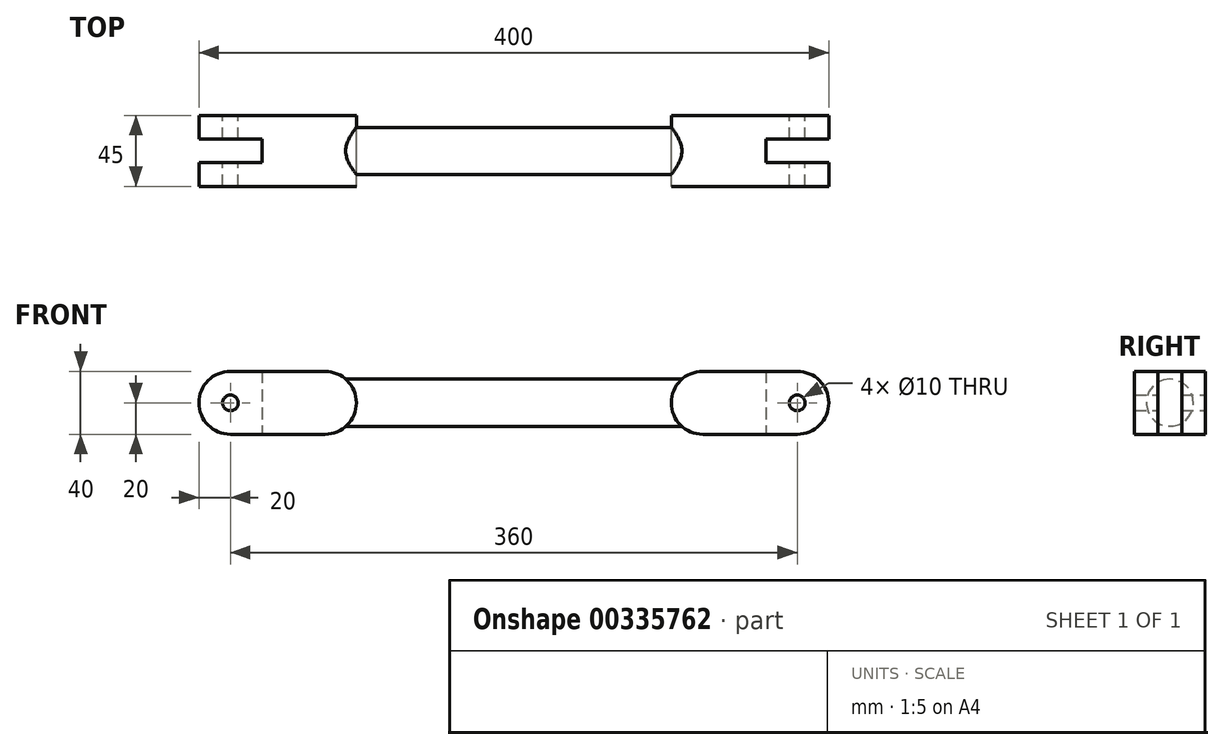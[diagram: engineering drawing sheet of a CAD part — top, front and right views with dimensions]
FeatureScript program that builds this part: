
annotation { "Feature Type Name" : "Feature", "Feature Type Description" : "" }
export const myFeature = defineFeature(function(context is Context, id is Id, definition is map)
    precondition{}
    {
        {
            var Q0;
            Q0=qCreatedBy(makeId("Front.planeOp"),FACE);
            var sketch = newSketch(context, id + "F0", { "sketchPlane" : qUnion([Q0])});
            skCircle(sketch, "E0", {"center": v(-180, 0) * mm, "radius": 20 * mm});
            skCircle(sketch, "E1", {"center": v(-120, 0) * mm, "radius": 20 * mm});
            skLineSegment(sketch, "E2", {"start": v(-180, 20) * mm, "end": v(-120, 20) * mm});
            skLineSegment(sketch, "E3", {"start": v(-180, -20) * mm, "end": v(-120, -20) * mm});
            skLineSegment(sketch, "E4", {"start": v(-180, 0) * mm, "end": v(-120, 0) * mm, "construction": true});
            skPoint(sketch, "E5", {"position": v(-150, 0) * mm});
            skCircle(sketch, "E6", {"center": v(-180, 0) * mm, "radius": 5 * mm});
            skSolve(sketch);
        }
        {
            var Q0;
            Q0=makeQuery(id+"F0.imprint","IMPRINT",FACE,{"disambiguationData":[TD([[makeQuery(id+"F0.imprint","IMPRINT",EDGE,{"derivedFrom":sQuery(id+"F0.wireOp",EDGE,"E6")}),-1.0]])]});
            var Q1;
            {var subQ0=sQuery(id+"F0.wireOp",EDGE,"E2");Q1=makeQuery(id+"F0.imprint","IMPRINT",FACE,{"disambiguationData":[TD([[makeQuery(id+"F0.imprint","IMPRINT",EDGE,{"derivedFrom":subQ0}),-1.0]])]});}
            var Q2;
            {var subQ0=sQuery(id+"F0.wireOp",EDGE,"E1");var subQ1=makeQuery(id+"F0.imprint","INTERSECT",VERTEX,{"derivedFrom":[subQ0,sQuery(id+"F0.wireOp",EDGE,"E2")]});Q2=makeQuery(id+"F0.imprint","IMPRINT",FACE,{"disambiguationData":[TD([[makeQuery(id+"F0.imprint","IMPRINT",EDGE,{"disambiguationData":[TD([[subQ1,-1.0]])],"derivedFrom":subQ0}),1.0]])]});}
            extrude(context, id + "F1", {"entities" : qUnion([Q0, Q1, Q2]), "depth" : 45 * mm, "symmetric" : true});
        }
        {
            var Q0;
            Q0=qCreatedBy(makeId("Top.planeOp"),FACE);
            var sketch = newSketch(context, id + "F2", { "sketchPlane" : qUnion([Q0])});
            skLineSegment(sketch, "E7.bottom", {"start": v(-160, 7.5) * mm, "end": v(-240, 7.5) * mm});
            skLineSegment(sketch, "E7.top", {"start": v(-160, -7.5) * mm, "end": v(-240, -7.5) * mm});
            skLineSegment(sketch, "E7.left", {"start": v(-160, 7.5) * mm, "end": v(-160, -7.5) * mm});
            skLineSegment(sketch, "E7.right", {"start": v(-240, 7.5) * mm, "end": v(-240, -7.5) * mm});
            skPoint(sketch, "E7.middle", {"position": v(-200, 0) * mm});
            skSolve(sketch);
        }
        {
            var Q0;
            Q0=makeQuery(id+"F2.imprint","IMPRINT",FACE,{"disambiguationData":[TD([[makeQuery(id+"F2.imprint","IMPRINT",EDGE,{"derivedFrom":sQuery(id+"F2.wireOp",EDGE,"E7.bottom")}),1.0]])]});
            extrude(context, id + "F3", {"entities" : qUnion([Q0]), "operationType" : NewBodyOperationType.REMOVE, "depth" : 73.4 * mm, "symmetric" : true});
        }
        {
            var Q0;
            Q0=makeQuery(id+"F1.opExtrude","SWEPT_BODY",BODY,{"disambiguationData":[OSD([sQuery(id+"F0.wireOp",EDGE,"E0"),sQuery(id+"F0.wireOp",EDGE,"E1"),sQuery(id+"F0.wireOp",EDGE,"E2"),sQuery(id+"F0.wireOp",EDGE,"E3"),sQuery(id+"F0.wireOp",EDGE,"E6")])]});
            var Q1;
            Q1=qCreatedBy(makeId("Right.planeOp"),FACE);
            mirror(context, id + "F4", {"entities" : qUnion([Q0]), "mirrorPlane" : qUnion([Q1])});
        }
        {
            var Q0;
            Q0=qCreatedBy(makeId("Right.planeOp"),FACE);
            var sketch = newSketch(context, id + "F5", { "sketchPlane" : qUnion([Q0])});
            skCircle(sketch, "E8", {"center": v(0, 0) * mm, "radius": 15 * mm});
            skSolve(sketch);
        }
        {
            var Q0;
            Q0=makeQuery(id+"F5.imprint","IMPRINT",FACE,{"disambiguationData":[TD([[makeQuery(id+"F5.imprint","IMPRINT",EDGE,{"derivedFrom":sQuery(id+"F5.wireOp",EDGE,"E8")}),1.0]])]});
            extrude(context, id + "F6", {"entities" : qUnion([Q0]), "endBound" : BoundingType.UP_TO_NEXT, "depth" : 25 * mm, "hasSecondDirection" : true, "secondDirectionBound" : BoundingType.UP_TO_NEXT, "secondDirectionOppositeDirection" : true, "secondDirectionDepth" : 25 * mm});
        }
    });
